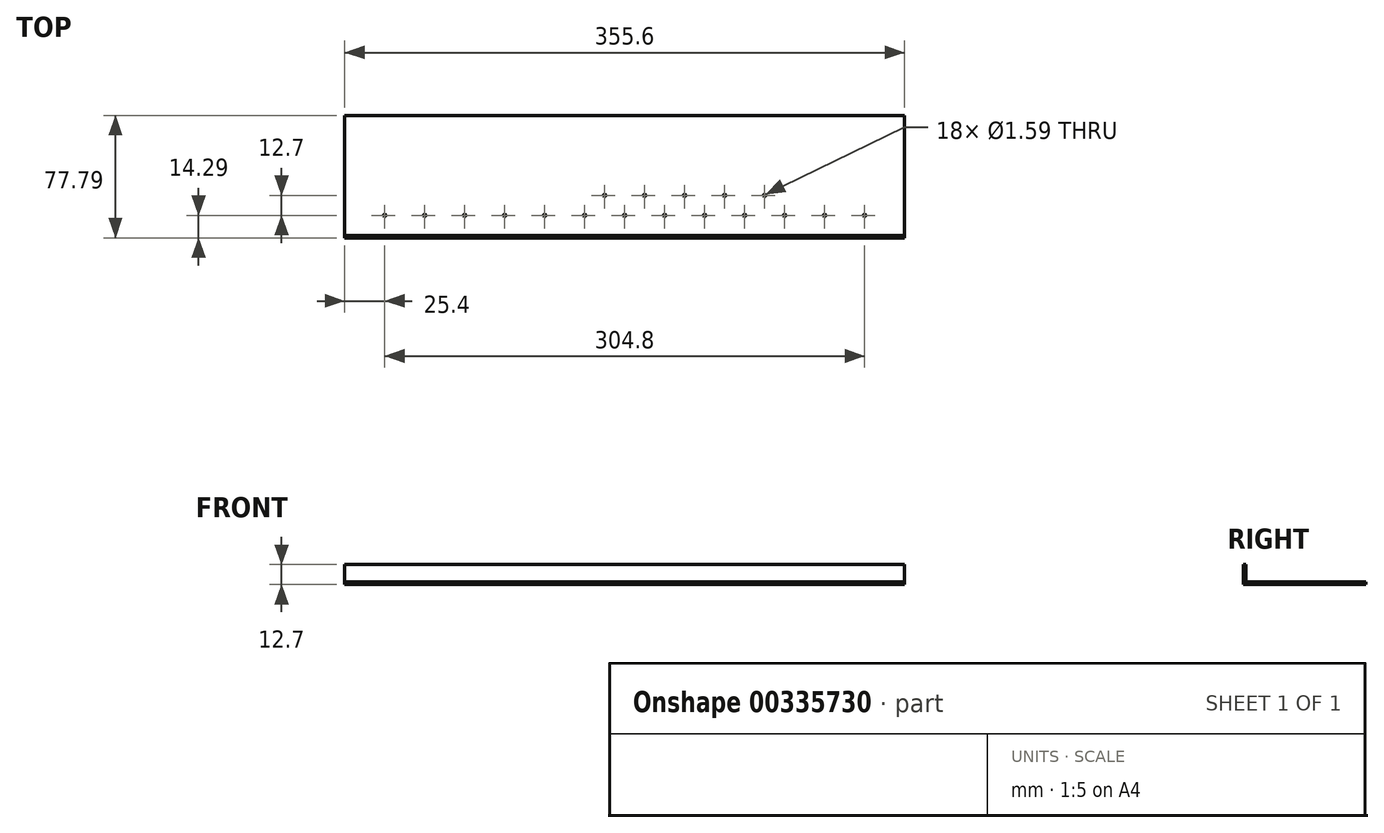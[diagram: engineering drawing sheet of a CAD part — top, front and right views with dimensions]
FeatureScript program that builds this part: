
annotation { "Feature Type Name" : "Feature", "Feature Type Description" : "" }
export const myFeature = defineFeature(function(context is Context, id is Id, definition is map)
    precondition{}
    {
        {
            var Q0;
            Q0=qCreatedBy(makeId("Top.planeOp"),FACE);
            var sketch = newSketch(context, id + "F0", { "sketchPlane" : qUnion([Q0])});
            skLineSegment(sketch, "E0.bottom", {"start": v(-177.8, -38.1) * mm, "end": v(177.8, -38.1) * mm});
            skLineSegment(sketch, "E0.top", {"start": v(-177.8, 38.1) * mm, "end": v(177.8, 38.1) * mm});
            skLineSegment(sketch, "E0.left", {"start": v(-177.8, -38.1) * mm, "end": v(-177.8, 38.1) * mm});
            skLineSegment(sketch, "E0.right", {"start": v(177.8, -38.1) * mm, "end": v(177.8, 38.1) * mm});
            skPoint(sketch, "E0.middle", {"position": v(0, 0) * mm});
            skLineSegment(sketch, "E1.top", {"start": v(-177.8, -39.69) * mm, "end": v(177.8, -39.69) * mm});
            skLineSegment(sketch, "E1.left", {"start": v(-177.8, -38.1) * mm, "end": v(-177.8, -39.69) * mm});
            skLineSegment(sketch, "E1.right", {"start": v(177.8, -38.1) * mm, "end": v(177.8, -39.69) * mm});
            skPoint(sketch, "E2", {"position": v(0, -25.4) * mm});
            skPoint(sketch, "E3", {"position": v(25.4, -25.4) * mm});
            skPoint(sketch, "E4", {"position": v(50.8, -25.4) * mm});
            skPoint(sketch, "E5", {"position": v(76.2, -25.4) * mm});
            skPoint(sketch, "E6", {"position": v(101.6, -25.4) * mm});
            skPoint(sketch, "E7", {"position": v(127, -25.4) * mm});
            skPoint(sketch, "E8", {"position": v(-25.4, -25.4) * mm});
            skPoint(sketch, "E9", {"position": v(152.4, -25.4) * mm});
            skPoint(sketch, "E10", {"position": v(-50.8, -25.4) * mm});
            skPoint(sketch, "E11", {"position": v(-76.2, -25.4) * mm});
            skPoint(sketch, "E12", {"position": v(-101.6, -25.4) * mm});
            skPoint(sketch, "E13", {"position": v(-127, -25.4) * mm});
            skPoint(sketch, "E14", {"position": v(-152.4, -25.4) * mm});
            skPoint(sketch, "E15", {"position": v(-12.7, -12.7) * mm});
            skPoint(sketch, "E16", {"position": v(12.7, -12.7) * mm});
            skPoint(sketch, "E17", {"position": v(38.1, -12.7) * mm});
            skPoint(sketch, "E18", {"position": v(63.5, -12.7) * mm});
            skPoint(sketch, "E19", {"position": v(88.9, -12.7) * mm});
            skSolve(sketch);
        }
        {
            var Q0;
            Q0=makeQuery(id+"F0.imprint","IMPRINT",FACE,{"disambiguationData":[TD([[makeQuery(id+"F0.imprint","IMPRINT",EDGE,{"derivedFrom":sQuery(id+"F0.wireOp",EDGE,"E0.bottom")}),-1.0]])]});
            extrude(context, id + "F1", {"entities" : qUnion([Q0]), "depth" : 12.7 * mm});
        }
        {
            var Q0;
            Q0 = qSketchRegion(id + "F0", true);
            extrude(context, id + "F2", {"entities" : qUnion([Q0]), "depth" : 1.59 * mm});
        }
        {
            var Q0;
            Q0=sQuery(id+"F0.wireOp",VERTEX,"E2");
            var Q1;
            Q1=sQuery(id+"F0.wireOp",VERTEX,"E8");
            var Q2;
            Q2=sQuery(id+"F0.wireOp",VERTEX,"E10");
            var Q3;
            Q3=sQuery(id+"F0.wireOp",VERTEX,"E11");
            var Q4;
            Q4=sQuery(id+"F0.wireOp",VERTEX,"E4");
            var Q5;
            Q5=sQuery(id+"F0.wireOp",VERTEX,"E3");
            var Q6;
            Q6=sQuery(id+"F0.wireOp",VERTEX,"E5");
            var Q7;
            Q7=sQuery(id+"F0.wireOp",VERTEX,"E6");
            var Q8;
            Q8=sQuery(id+"F0.wireOp",VERTEX,"E7");
            var Q9;
            Q9=sQuery(id+"F0.wireOp",VERTEX,"E9");
            var Q10;
            Q10=sQuery(id+"F0.wireOp",VERTEX,"E12");
            var Q11;
            Q11=sQuery(id+"F0.wireOp",VERTEX,"E13");
            var Q12;
            Q12=sQuery(id+"F0.wireOp",VERTEX,"E14");
            var Q13;
            Q13=sQuery(id+"F0.wireOp",VERTEX,"E15");
            var Q14;
            Q14=sQuery(id+"F0.wireOp",VERTEX,"E16");
            var Q15;
            Q15=sQuery(id+"F0.wireOp",VERTEX,"E17");
            var Q16;
            Q16=sQuery(id+"F0.wireOp",VERTEX,"E18");
            var Q17;
            Q17=sQuery(id+"F0.wireOp",VERTEX,"E19");
            var Q18;
            Q18=makeQuery(id+"F2.opExtrude","SWEPT_BODY",BODY,{"disambiguationData":[OSD([sQuery(id+"F0.wireOp",EDGE,"E0.top"),sQuery(id+"F0.wireOp",EDGE,"E0.left"),sQuery(id+"F0.wireOp",EDGE,"E0.right"),sQuery(id+"F0.wireOp",EDGE,"E1.top"),sQuery(id+"F0.wireOp",EDGE,"E1.left"),sQuery(id+"F0.wireOp",EDGE,"E1.right")])]});
            hole(context, id + "F3", {"style" : HoleStyle.SIMPLE, "endStyle" : HoleEndStyle.THROUGH, "oppositeDirection" : true, "holeDiameter" : 1.59 * mm, "tappedDepth" : 12.7 * mm, "tapClearance" : 3, "locations" : qUnion([Q0, Q1, Q2, Q3, Q4, Q5, Q6, Q7, Q8, Q9, Q10, Q11, Q12, Q13, Q14, Q15, Q16, Q17]), "scope" : qUnion([Q18])});
        }
    });
